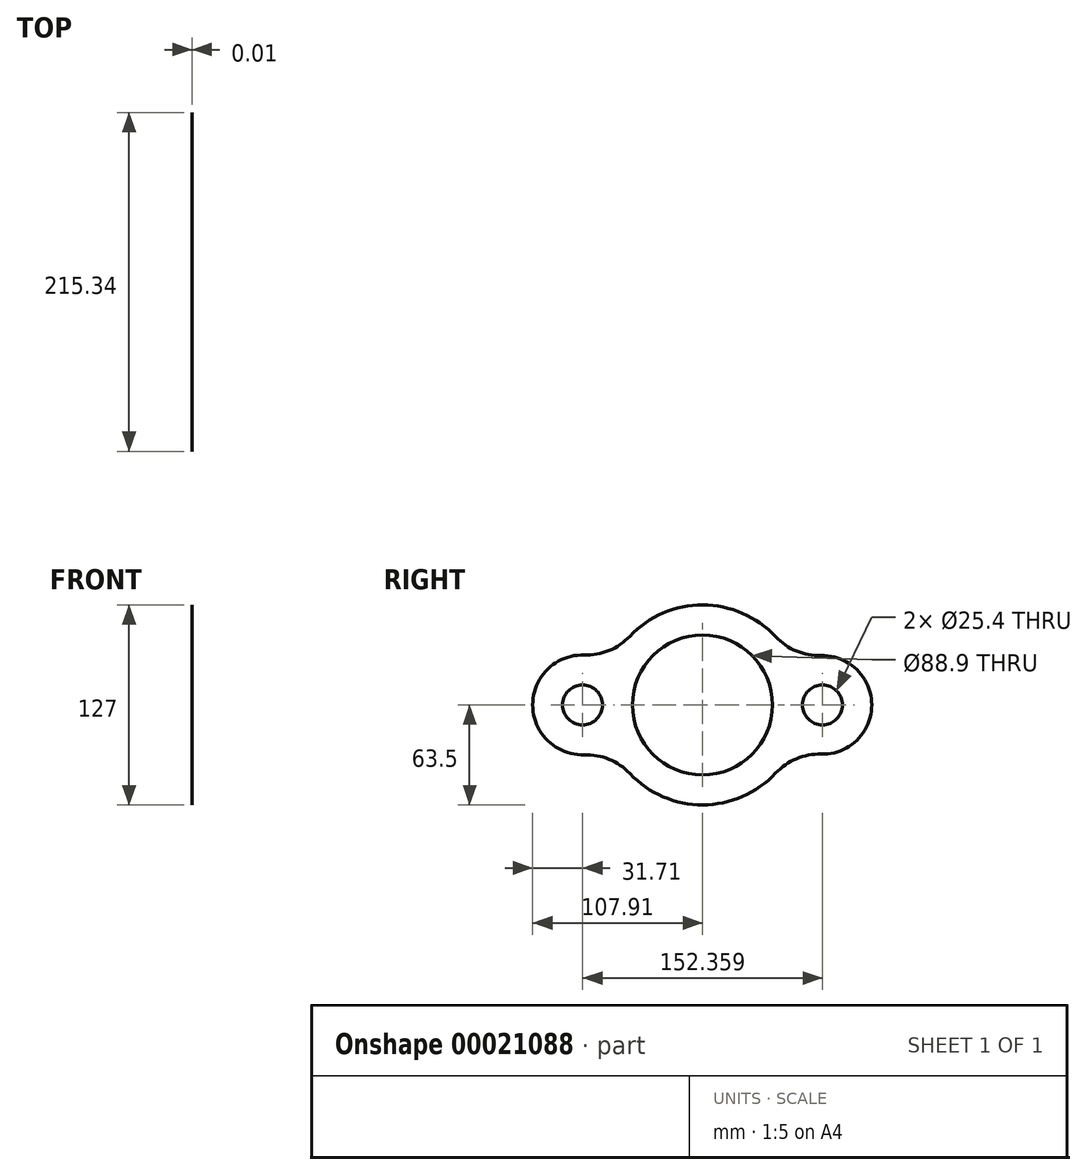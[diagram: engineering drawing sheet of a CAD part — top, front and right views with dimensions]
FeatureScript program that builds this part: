
annotation { "Feature Type Name" : "Feature", "Feature Type Description" : "" }
export const myFeature = defineFeature(function(context is Context, id is Id, definition is map)
    precondition{}
    {
        {
            var Q0;
            Q0=qCreatedBy(makeId("Right.planeOp"),FACE);
            var sketch = newSketch(context, id + "F0", { "sketchPlane" : qUnion([Q0])});
            skCircle(sketch, "E0", {"center": v(0, 0) * mm, "radius": 44.45 * mm});
            skArc(sketch, "E1", {"start": v(46.4, 43.34) * mm, "mid": v(0.18, 63.5) * mm, "end": v(-46.16, 43.6) * mm});
            skLineSegment(sketch, "E2", {"start": v(-63.5, 0) * mm, "end": v(-76.2, 0) * mm});
            skArc(sketch, "E3", {"start": v(-75.14, 31.69) * mm, "mid": v(-107.9, 0) * mm, "end": v(-75.14, -31.69) * mm});
            skArc(sketch, "E4", {"start": v(75.3, -31.26) * mm, "mid": v(107.43, 0) * mm, "end": v(75.3, 31.26) * mm});
            skCircle(sketch, "E5", {"center": v(-76.2, 0) * mm, "radius": 12.7 * mm});
            skCircle(sketch, "E6", {"center": v(76.16, 0) * mm, "radius": 12.7 * mm});
            skArc(sketch, "E7.trimOffspring", {"start": v(63.5, -0.93) * mm, "mid": v(63.5, 0) * mm, "end": v(63.5, 0.93) * mm});
            skArc(sketch, "E8.trimOffspring", {"start": v(-46.16, -43.6) * mm, "mid": v(0.18, -63.5) * mm, "end": v(46.4, -43.34) * mm});
            skPoint(sketch, "E9.visualSharp", {"position": v(-57.96, 25.94) * mm});
            skArc(sketch, "E9.filletArc", {"start": v(-75.14, 31.69) * mm, "mid": v(-59.37, 34.53) * mm, "end": v(-46.16, 43.6) * mm});
            skPoint(sketch, "E10.visualSharp", {"position": v(58.13, 25.55) * mm});
            skArc(sketch, "E10.filletArc", {"start": v(46.4, 43.34) * mm, "mid": v(59.56, 34.2) * mm, "end": v(75.3, 31.26) * mm});
            skPoint(sketch, "E11.visualSharp", {"position": v(58.13, -25.55) * mm});
            skArc(sketch, "E11.filletArc", {"start": v(75.3, -31.26) * mm, "mid": v(59.56, -34.2) * mm, "end": v(46.4, -43.34) * mm});
            skPoint(sketch, "E12.visualSharp", {"position": v(-57.96, -25.94) * mm});
            skArc(sketch, "E12.filletArc", {"start": v(-46.16, -43.6) * mm, "mid": v(-59.37, -34.53) * mm, "end": v(-75.14, -31.69) * mm});
            skSolve(sketch);
        }
        {
            var Q0;
            Q0=makeQuery(id+"F0.imprint","IMPRINT",FACE,{"disambiguationData":[TD([[makeQuery(id+"F0.imprint","IMPRINT",EDGE,{"derivedFrom":sQuery(id+"F0.wireOp",EDGE,"E0")}),-1.0]])]});
            extrude(context, id + "F1", {"entities" : qUnion([Q0]), "depth" : 1 / 101.6 * mm});
        }
    });
